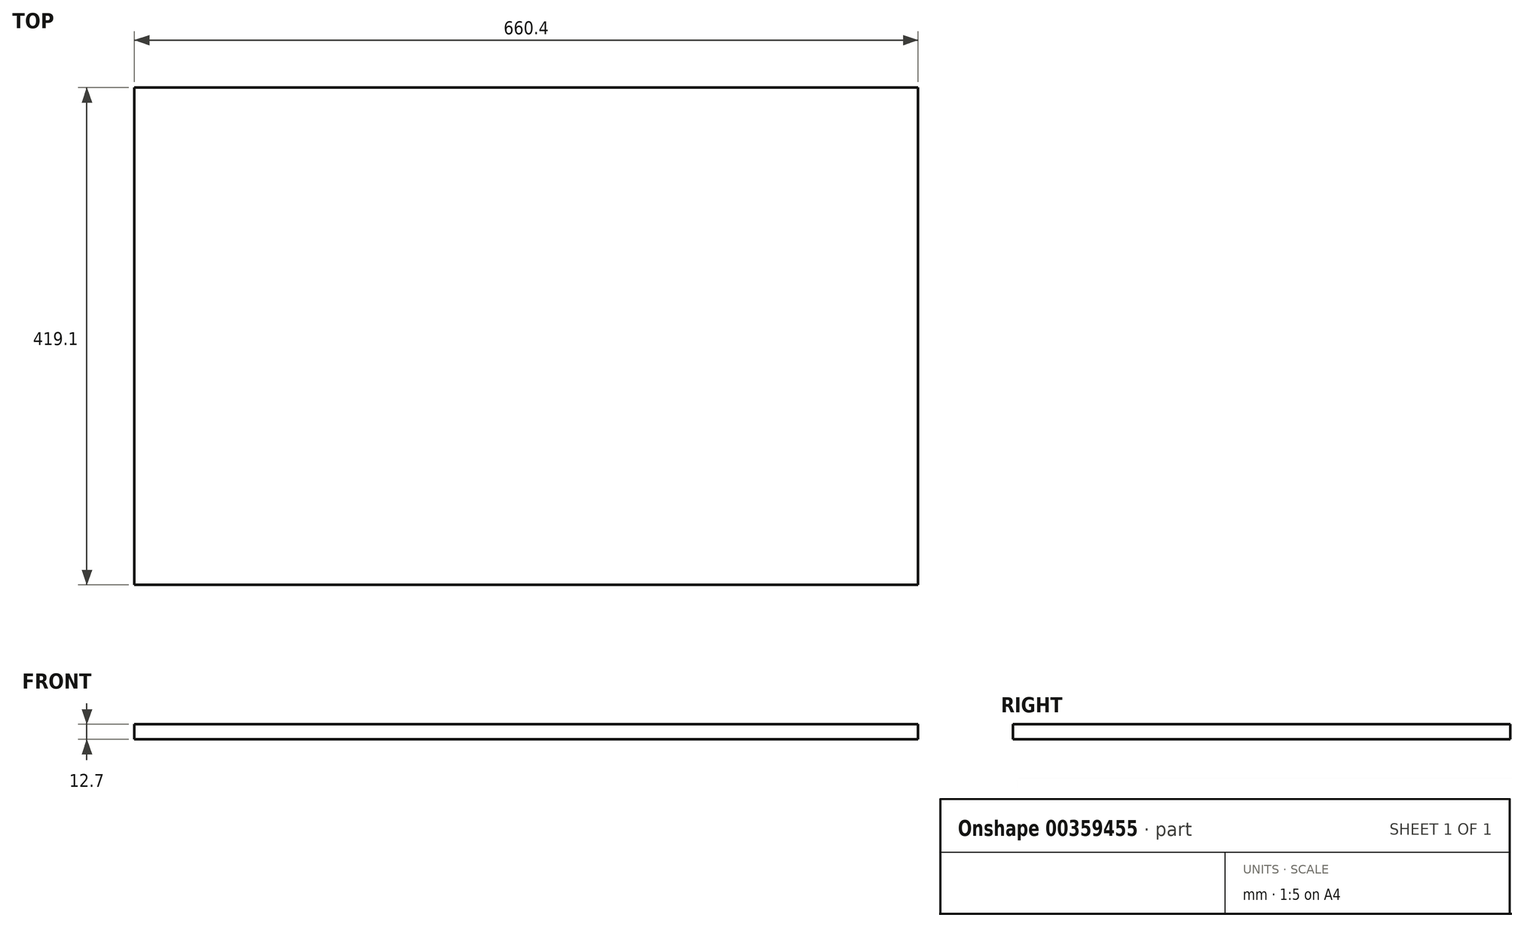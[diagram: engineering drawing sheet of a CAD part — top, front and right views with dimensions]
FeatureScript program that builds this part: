
annotation { "Feature Type Name" : "Feature", "Feature Type Description" : "" }
export const myFeature = defineFeature(function(context is Context, id is Id, definition is map)
    precondition{}
    {
        {
            var Q0;
            Q0=qCreatedBy(makeId("Top.planeOp"),FACE);
            var sketch = newSketch(context, id + "F0", { "sketchPlane" : qUnion([Q0])});
            skLineSegment(sketch, "E0.bottom", {"start": v(0, 0) * mm, "end": v(660.4, 0) * mm});
            skLineSegment(sketch, "E0.top", {"start": v(0, 419.1) * mm, "end": v(660.4, 419.1) * mm});
            skLineSegment(sketch, "E0.left", {"start": v(0, 0) * mm, "end": v(0, 419.1) * mm});
            skLineSegment(sketch, "E0.right", {"start": v(660.4, 0) * mm, "end": v(660.4, 419.1) * mm});
            skSolve(sketch);
        }
        {
            var Q0;
            Q0=makeQuery(id+"F0.imprint","IMPRINT",FACE,{"disambiguationData":[TD([[makeQuery(id+"F0.imprint","IMPRINT",EDGE,{"derivedFrom":sQuery(id+"F0.wireOp",EDGE,"E0.bottom")}),1.0]])]});
            extrude(context, id + "F1", {"entities" : qUnion([Q0]), "depth" : 12.7 * mm});
        }
    });
